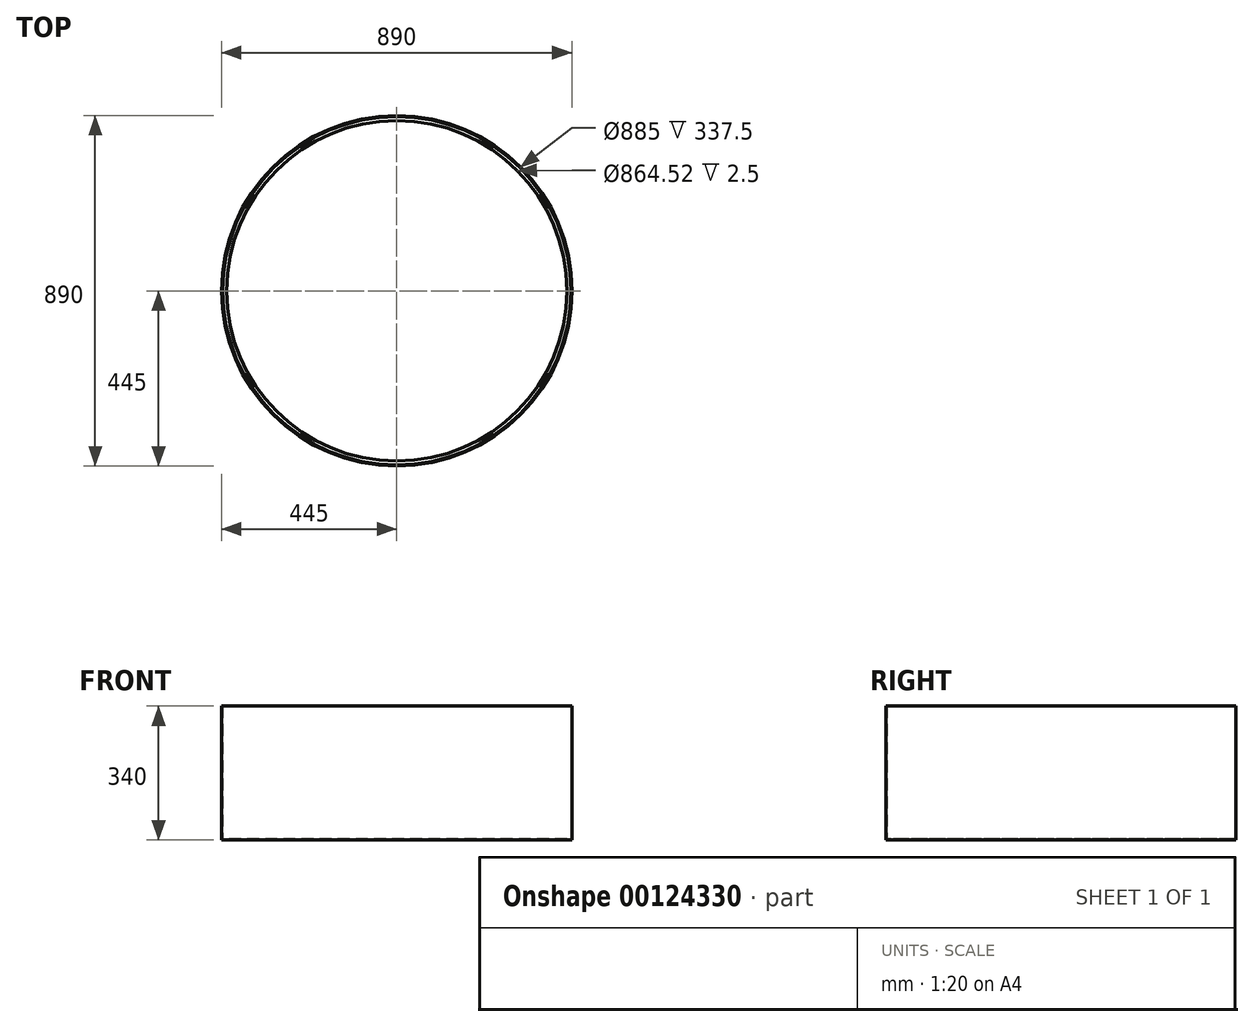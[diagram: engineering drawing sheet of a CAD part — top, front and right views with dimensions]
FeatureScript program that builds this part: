
annotation { "Feature Type Name" : "Feature", "Feature Type Description" : "" }
export const myFeature = defineFeature(function(context is Context, id is Id, definition is map)
    precondition{}
    {
        {
            var Q0;
            Q0=qCreatedBy(makeId("Right.planeOp"),FACE);
            var sketch = newSketch(context, id + "F0", { "sketchPlane" : qUnion([Q0])});
            skLineSegment(sketch, "E0", {"start": v(0, 0) * mm, "end": v(-220, 0) * mm});
            skLineSegment(sketch, "E1", {"start": v(-220, 0) * mm, "end": v(-220, 50) * mm});
            skLineSegment(sketch, "E2", {"start": v(-220, 50) * mm, "end": v(-320, 50) * mm});
            skLineSegment(sketch, "E3", {"start": v(-320, 50) * mm, "end": v(-320, 0) * mm});
            skLineSegment(sketch, "E4", {"start": v(-320, 0) * mm, "end": v(-445, 0) * mm});
            skLineSegment(sketch, "E5", {"start": v(-445, 0) * mm, "end": v(-445, 340) * mm});
            skLineSegment(sketch, "E6", {"start": v(-445, 340) * mm, "end": v(0, 340) * mm});
            skLineSegment(sketch, "E7", {"start": v(0, 0) * mm, "end": v(0, 340) * mm});
            skLineSegment(sketch, "E8", {"start": v(-220, 0) * mm, "end": v(-320, 0) * mm});
            skSolve(sketch);
        }
        {
            var Q0;
            Q0=makeQuery(id+"F0.imprint","IMPRINT",FACE,{"disambiguationData":[TD([[makeQuery(id+"F0.imprint","IMPRINT",EDGE,{"derivedFrom":sQuery(id+"F0.wireOp",EDGE,"E0")}),-1.0]])]});
            var Q1;
            Q1=makeQuery(id+"F0.imprint","IMPRINT",FACE,{"disambiguationData":[TD([[makeQuery(id+"F0.imprint","IMPRINT",EDGE,{"derivedFrom":sQuery(id+"F0.wireOp",EDGE,"E1")}),1.0]])]});
            var Q2;
            Q2=sQuery(id+"F0.wireOp",EDGE,"E7");
            revolve(context, id + "F1", {"entities" : qUnion([Q0, Q1]), "axis" : qUnion([Q2]), "revolveType" : RevolveType.FULL});
        }
        {
            var Q0;
            Q0=makeQuery(id+"F1.opRevolve","SWEPT_FACE",FACE,{"disambiguationData":[OSD([sQuery(id+"F0.wireOp",EDGE,"E6")])]});
            shell(context, id + "F2", {"entities" : qUnion([Q0]), "thickness" : 2.5 * mm});
        }
        {
            var Q0;
            Q0=makeQuery(id+"F2.opShell","OFFSET_FACE",FACE,{"disambiguationData":[OSD([sQuery(id+"F0.wireOp",EDGE,"E0"),sQuery(id+"F0.wireOp",EDGE,"E4"),sQuery(id+"F0.wireOp",EDGE,"E8")])]});
            var sketch = newSketch(context, id + "F3", { "sketchPlane" : qUnion([Q0])});
            skCircle(sketch, "E9", {"center": v(0, 0) * mm, "radius": 432.26 * mm});
            skSolve(sketch);
        }
        {
            var Q0;
            Q0=makeQuery(id+"F3.imprint","IMPRINT",FACE,{"disambiguationData":[TD([[makeQuery(id+"F3.imprint","IMPRINT",EDGE,{"derivedFrom":sQuery(id+"F3.wireOp",EDGE,"E9")}),1.0]])]});
            extrude(context, id + "F4", {"entities" : qUnion([Q0]), "operationType" : NewBodyOperationType.REMOVE, "endBound" : BoundingType.THROUGH_ALL, "oppositeDirection" : true, "depth" : 25 * mm});
        }
    });
